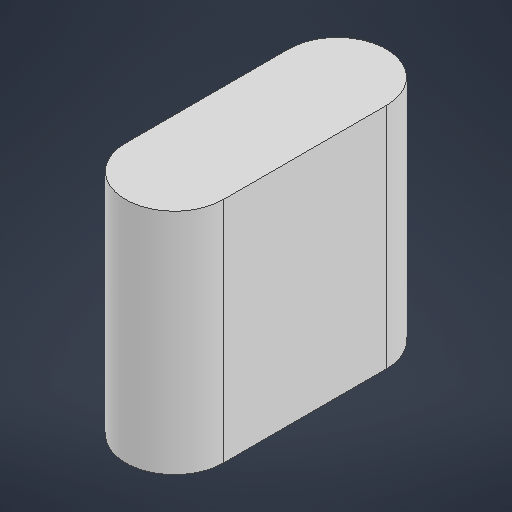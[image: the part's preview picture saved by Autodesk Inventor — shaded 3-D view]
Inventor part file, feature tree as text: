
AUTODESK INVENTOR PART (.ipt)
format: ipt  version: 2025.3 (Build 293356000, 356)  size: 204,800 bytes
history: native  units: mm
features: extrude x2, sketch x2, plane x1, projected_geometry x1
ambient origin geometry x8: Origin, YZ Plane, XZ Plane, XY Plane, X Axis, Y Axis, Z Axis, Center Point
bodies: Solid1 (feature_tree)
feature tree (6):
  extrude  "Extrusion1"  Depth=3.0mm
  plane  "Work Plane2"
  extrude  "Extrusion3"  Depth=3.0mm
  sketch  "Sketch1"  dims[d0=10.0mm d1=3.0mm]
  sketch  "Sketch3"  dims[d3=14.0mm d4=0.0mm d12=3.0mm d13=7.0mm d14=3.0mm d15=5.0mm d16=0.0mm d5=0.5mm d6=0.872665mm]
  projected_geometry  "Projected Loop1"
